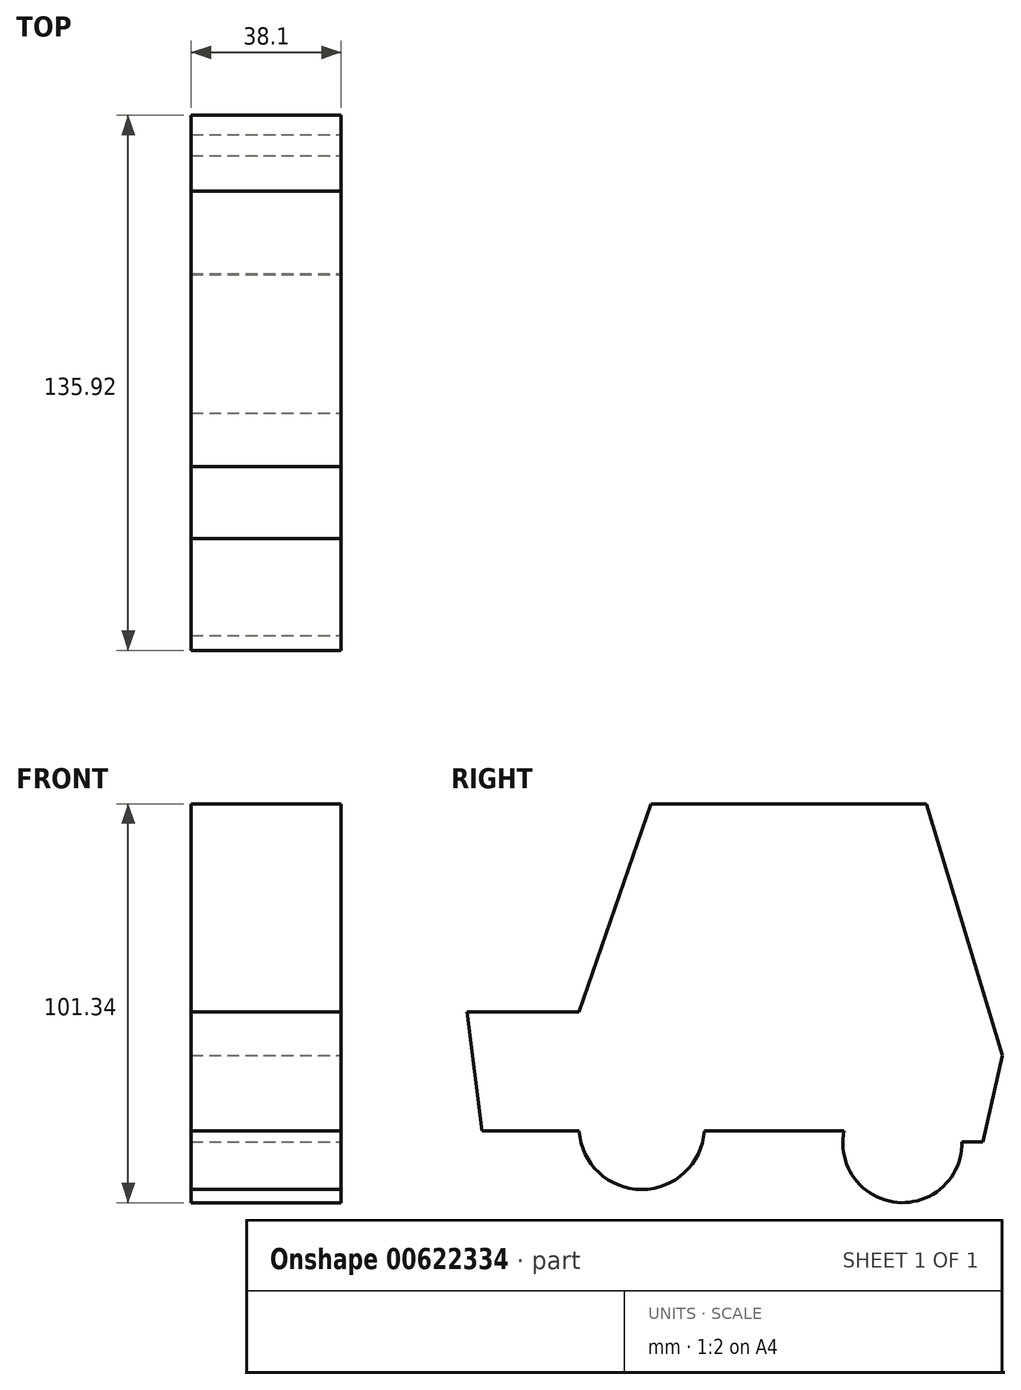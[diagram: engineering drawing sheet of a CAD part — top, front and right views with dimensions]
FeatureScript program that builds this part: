
annotation { "Feature Type Name" : "Feature", "Feature Type Description" : "" }
export const myFeature = defineFeature(function(context is Context, id is Id, definition is map)
    precondition{}
    {
        {
            var Q0;
            Q0=qCreatedBy(makeId("Right.planeOp"),FACE);
            var sketch = newSketch(context, id + "F0", { "sketchPlane" : qUnion([Q0])});
            skLineSegment(sketch, "E0", {"start": v(-25.25, 52.9) * mm, "end": v(44.8, 52.9) * mm});
            skLineSegment(sketch, "E1", {"start": v(44.8, 52.9) * mm, "end": v(64.02, -11.04) * mm});
            skLineSegment(sketch, "E2", {"start": v(64.02, -11.04) * mm, "end": v(59.08, -32.98) * mm});
            skLineSegment(sketch, "E3", {"start": v(59.08, -32.98) * mm, "end": v(53.83, -32.98) * mm});
            skLineSegment(sketch, "E4", {"start": v(-25.25, 52.9) * mm, "end": v(-43.48, 0) * mm});
            skLineSegment(sketch, "E5", {"start": v(-43.48, 0) * mm, "end": v(-71.9, 0) * mm});
            skLineSegment(sketch, "E6", {"start": v(-71.9, 0) * mm, "end": v(-68.2, -30.2) * mm});
            skLineSegment(sketch, "E7", {"start": v(-68.2, -30.2) * mm, "end": v(-43.48, -30.2) * mm});
            skArc(sketch, "E8", {"start": v(-43.48, -30.2) * mm, "mid": v(-27.57, -45.1) * mm, "end": v(-11.66, -30.2) * mm});
            skLineSegment(sketch, "E9", {"start": v(-11.66, -30.2) * mm, "end": v(23.86, -30.2) * mm});
            skArc(sketch, "E10", {"start": v(23.86, -30.2) * mm, "mid": v(37.29, -48.37) * mm, "end": v(53.83, -32.98) * mm});
            skSolve(sketch);
        }
        {
            var Q0;
            Q0=makeQuery(id+"F0.imprint","IMPRINT",FACE,{"disambiguationData":[TD([[makeQuery(id+"F0.imprint","IMPRINT",EDGE,{"derivedFrom":sQuery(id+"F0.wireOp",EDGE,"E0")}),-1.0]])]});
            extrude(context, id + "F1", {"entities" : qUnion([Q0]), "oppositeDirection" : true, "depth" : 38.1 * mm, "offsetDistance" : 25.4 * mm});
        }
    });
